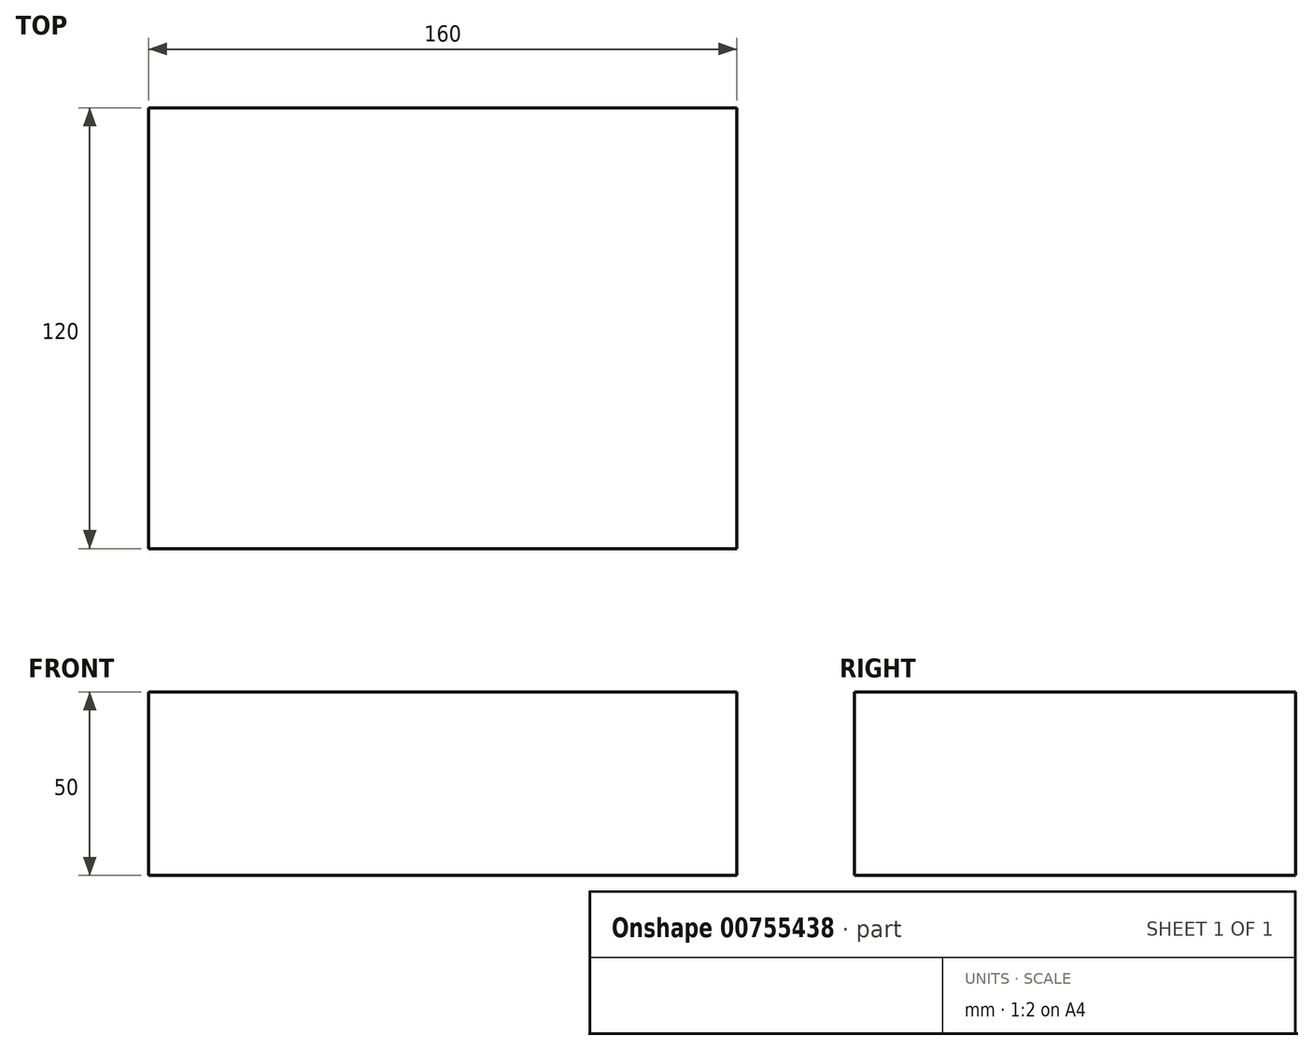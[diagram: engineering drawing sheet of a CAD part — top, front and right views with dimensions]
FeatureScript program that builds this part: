
annotation { "Feature Type Name" : "Feature", "Feature Type Description" : "" }
export const myFeature = defineFeature(function(context is Context, id is Id, definition is map)
    precondition{}
    {
        {
            var Q0;
            Q0=qCreatedBy(makeId("Top.planeOp"),FACE);
            var sketch = newSketch(context, id + "F0", { "sketchPlane" : qUnion([Q0])});
            skLineSegment(sketch, "E0.bottom", {"start": v(-80, -60) * mm, "end": v(80, -60) * mm});
            skLineSegment(sketch, "E0.top", {"start": v(-80, 60) * mm, "end": v(80, 60) * mm});
            skLineSegment(sketch, "E0.left", {"start": v(-80, -60) * mm, "end": v(-80, 60) * mm});
            skLineSegment(sketch, "E0.right", {"start": v(80, -60) * mm, "end": v(80, 60) * mm});
            skPoint(sketch, "E0.middle", {"position": v(0, 0) * mm});
            skSolve(sketch);
        }
        {
            var Q0;
            Q0 = qSketchRegion(id + "F0", true);
            extrude(context, id + "F1", {"entities" : qUnion([Q0]), "depth" : 50 * mm, "offsetDistance" : 25 * mm});
        }
    });
